# Revit family: HERZ Isolating Butterfly Valves AF-4219 with gearbox
name_source: partatom
category: Rohrzubehör
units: mm (PartAtom-declared; Revit-internal decimal feet)

## family parameters
Arbeitsebenenbasiert = Nein
Beim Laden mit Abzugskörper schneiden = Nein
Bemaßung runder Anschluss = Durchmesser verwenden
Gemeinsam genutzt = Nein
Immer vertikal = Ja
OmniClass-Nummer = 23.65.55.14
OmniClass-Titel = Valves for Liquid Services
Teiletyp = Unterbricht

## types (1)
- HERZ Isolating Butterfly Valves AF-4219 with gearbox
    Application = Suitable for fluids in building services, cold water systems, hot water saystems, etc.
    Body = GGG, GJS-400-15/JS1030, according to EN1563
    Body sealing = EPDM according to ISO 1691
    Disc = stainless steel 1.4408
    Flange = according to EN1092-2
    Hersteller = HERZ Armaturen Ges.m.b.H.
    Max. operating temperature = 110 °C
    Medium = Heating water quality according ÖNORM H5195 or VDI-Standard 2035. The use of ethylene or propylene glycol in a
mixing ratio 25- 50% is allowed.
    Min. operating temperature = -20.00 °C with appropriate water-glycol mixture
    O-Ring = EPDM according to ISO 1691
    R99 = 2 mm  [stored 0.00656168 ft]
    SCRNCODE = 05;13;02
    SCRNSEQ = ARM;ARM_TYP="ALLF";2
    SCTWCODE = 04;07;02
    SCTWSEQ = FW;SBT_TYP_FW="101";2
    Spindle = stainless steel ASTM-A276 / Type 316
    URL = www.herzvalves.com
    Vorgabe-Ansicht = 0 mm  [stored 0 ft]

note: [stored X ft] marks values corroborated as IEEE doubles in the binary element streams (Revit-internal decimal feet)
